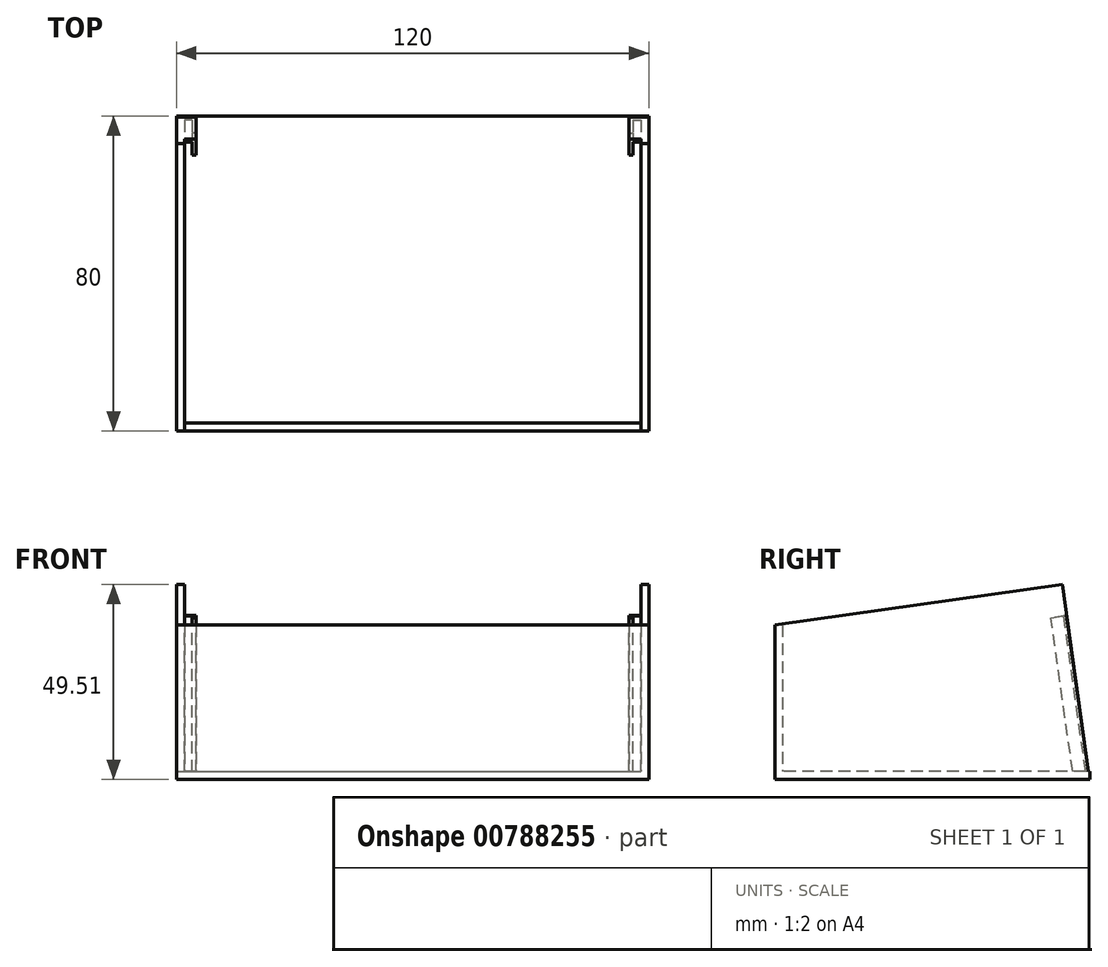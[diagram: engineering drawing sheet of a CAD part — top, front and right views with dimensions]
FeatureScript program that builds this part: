
annotation { "Feature Type Name" : "Feature", "Feature Type Description" : "" }
export const myFeature = defineFeature(function(context is Context, id is Id, definition is map)
    precondition{}
    {
        {
            var Q0;
            Q0=qCreatedBy(makeId("Top.planeOp"),FACE);
            var sketch = newSketch(context, id + "F0", { "sketchPlane" : qUnion([Q0])});
            skLineSegment(sketch, "E0.bottom", {"start": v(-60, 56.5) * mm, "end": v(60, 56.5) * mm});
            skLineSegment(sketch, "E0.top", {"start": v(-60, -23.5) * mm, "end": v(60, -23.5) * mm});
            skLineSegment(sketch, "E0.left", {"start": v(-60, 56.5) * mm, "end": v(-60, -23.5) * mm});
            skLineSegment(sketch, "E0.right", {"start": v(60, 56.5) * mm, "end": v(60, -23.5) * mm});
            skSolve(sketch);
        }
        {
            var Q0;
            Q0 = qSketchRegion(id + "F0", true);
            var Q1;
            Q1=makeQuery(id+"F0.imprint","IMPRINT",FACE,{"disambiguationData":[TD([[makeQuery(id+"F0.imprint","IMPRINT",EDGE,{"derivedFrom":sQuery(id+"F0.wireOp",EDGE,"E0.bottom")}),-1.0]])]});
            extrude(context, id + "F1", {"entities" : qUnion([Q0, Q1]), "depth" : 2 * mm, "offsetDistance" : 25 * mm});
        }
        {
            var Q0;
            Q0=makeQuery(id+"F1.opExtrude","SWEPT_FACE",FACE,{"disambiguationData":[OSD([sQuery(id+"F0.wireOp",EDGE,"E0.right")])]});
            var sketch = newSketch(context, id + "F2", { "sketchPlane" : qUnion([Q0])});
            skLineSegment(sketch, "E1", {"start": v(56.5, 0) * mm, "end": v(49.5, 49.5) * mm});
            skLineSegment(sketch, "E2", {"start": v(49.5, 49.5) * mm, "end": v(-23.5, 39.19) * mm});
            skLineSegment(sketch, "E3", {"start": v(-23.5, 39.19) * mm, "end": v(-23.5, 0) * mm});
            skSolve(sketch);
        }
        {
            var Q0;
            Q0 = qSketchRegion(id + "F2", true);
            var Q1;
            {var subQ0=sQuery(id+"F2.wireOp",EDGE,"E2");Q1=makeQuery(id+"F2.imprint","IMPRINT",FACE,{"disambiguationData":[TD([[makeQuery(id+"F2.imprint","IMPRINT",EDGE,{"derivedFrom":subQ0}),1.0]])]});}
            extrude(context, id + "F3", {"entities" : qUnion([Q0, Q1]), "operationType" : NewBodyOperationType.ADD, "oppositeDirection" : true, "depth" : 2 * mm, "offsetDistance" : 25 * mm});
        }
        {
            var Q0;
            Q0=makeQuery(id+"F1.opExtrude","SWEPT_BODY",BODY,{"disambiguationData":[OSD([sQuery(id+"F0.wireOp",EDGE,"E0.bottom"),sQuery(id+"F0.wireOp",EDGE,"E0.top"),sQuery(id+"F0.wireOp",EDGE,"E0.left"),sQuery(id+"F0.wireOp",EDGE,"E0.right")])]});
            var Q1;
            Q1=qCreatedBy(makeId("Right.planeOp"),FACE);
            mirror(context, id + "F4", {"operationType" : NewBodyOperationType.ADD, "entities" : qUnion([Q0]), "mirrorPlane" : qUnion([Q1])});
        }
        {
            var Q0;
            {var subQ0=makeQuery(id+"F3.boolean.opBoolean","MERGE",FACE,{"derivedFrom":[makeQuery(id+"F1.opExtrude","SWEPT_FACE",FACE,{"disambiguationData":[OSD([sQuery(id+"F0.wireOp",EDGE,"E0.top")])]}),makeQuery(id+"F3.opExtrude","SWEPT_FACE",FACE,{"disambiguationData":[OSD([sQuery(id+"F2.wireOp",EDGE,"E3")])]})]});Q0=makeQuery(id+"F4.boolean.opBoolean","MERGE",FACE,{"derivedFrom":[subQ0,makeQuery(id+"F4.opPattern","COPY",FACE,{"derivedFrom":subQ0,"instanceName":"1"})]});}
            var sketch = newSketch(context, id + "F5", { "sketchPlane" : qUnion([Q0])});
            skLineSegment(sketch, "E4", {"start": v(-60, 39.19) * mm, "end": v(-60, 0) * mm});
            skLineSegment(sketch, "E5", {"start": v(60, 39.19) * mm, "end": v(-60, 39.19) * mm});
            skSolve(sketch);
        }
        {
            var Q0;
            {var subQ1=makeQuery(id+"F3.opExtrude","CAP_EDGE",EDGE,{"disambiguationData":[OSD([sQuery(id+"F2.wireOp",EDGE,"E3")])],"isStart":false});Q0=makeQuery(id+"F5.imprint","IMPRINT",FACE,{"disambiguationData":[TD([[makeQuery(id+"F5.imprint","IMPRINT",EDGE,{"derivedFrom":subQ1}),-1.0]])]});}
            extrude(context, id + "F6", {"entities" : qUnion([Q0]), "operationType" : NewBodyOperationType.ADD, "oppositeDirection" : true, "depth" : 2 * mm, "offsetDistance" : 25 * mm});
        }
        {
            var Q0;
            Q0=makeQuery(id+"F4.opPattern","COPY",FACE,{"derivedFrom":makeQuery(id+"F3.opExtrude","CAP_FACE",FACE,{"disambiguationData":[OSD([sQuery(id+"F0.wireOp",EDGE,"E0.right"),sQuery(id+"F2.wireOp",EDGE,"E1"),sQuery(id+"F2.wireOp",EDGE,"E2"),sQuery(id+"F2.wireOp",EDGE,"E3")])],"isStart":false}),"instanceName":"1"});
            var sketch = newSketch(context, id + "F7", { "sketchPlane" : qUnion([Q0])});
            skLineSegment(sketch, "E6", {"start": v(56.22, 2) * mm, "end": v(50.62, 41.6) * mm});
            skLineSegment(sketch, "E7", {"start": v(50.62, 41.6) * mm, "end": v(46.66, 41.05) * mm});
            skLineSegment(sketch, "E8", {"start": v(46.66, 41.05) * mm, "end": v(52.18, 2) * mm});
            skSolve(sketch);
        }
        {
            var Q0;
            Q0 = qSketchRegion(id + "F7", true);
            var Q1;
            {var subQ0=sQuery(id+"F7.wireOp",EDGE,"E6");Q1=makeQuery(id+"F7.imprint","IMPRINT",FACE,{"disambiguationData":[TD([[makeQuery(id+"F7.imprint","IMPRINT",EDGE,{"derivedFrom":subQ0}),1.0]])]});}
            extrude(context, id + "F8", {"entities" : qUnion([Q0, Q1]), "operationType" : NewBodyOperationType.ADD, "depth" : 3 * mm, "offsetDistance" : 25 * mm});
        }
        {
            var Q0;
            Q0=makeQuery(id+"F8.opExtrude","SWEPT_FACE",FACE,{"disambiguationData":[OSD([sQuery(id+"F7.wireOp",EDGE,"E7")])]});
            var sketch = newSketch(context, id + "F9", { "sketchPlane" : qUnion([Q0])});
            skLineSegment(sketch, "E9.bottom", {"start": v(-58, 51.94) * mm, "end": v(-56, 51.94) * mm});
            skLineSegment(sketch, "E9.top", {"start": v(-58, 55.22) * mm, "end": v(-56, 55.22) * mm});
            skLineSegment(sketch, "E9.left", {"start": v(-58, 51.94) * mm, "end": v(-58, 55.22) * mm});
            skLineSegment(sketch, "E9.right", {"start": v(-56, 51.94) * mm, "end": v(-56, 55.22) * mm});
            skSolve(sketch);
        }
        {
            var Q0;
            Q0=makeQuery(id+"F9.imprint","IMPRINT",FACE,{"disambiguationData":[TD([[makeQuery(id+"F9.imprint","IMPRINT",EDGE,{"derivedFrom":sQuery(id+"F9.wireOp",EDGE,"E9.bottom")}),-1.0]])]});
            var Q1;
            Q1=makeQuery(id+"F1.opExtrude","CAP_FACE",FACE,{"disambiguationData":[OSD([sQuery(id+"F0.wireOp",EDGE,"E0.bottom"),sQuery(id+"F0.wireOp",EDGE,"E0.top"),sQuery(id+"F0.wireOp",EDGE,"E0.left"),sQuery(id+"F0.wireOp",EDGE,"E0.right")])],"isStart":false});
            extrude(context, id + "F10", {"entities" : qUnion([Q0]), "operationType" : NewBodyOperationType.REMOVE, "endBound" : BoundingType.UP_TO_SURFACE, "oppositeDirection" : true, "depth" : 25 * mm, "endBoundEntityFace" : qUnion([Q1]), "offsetDistance" : 25 * mm});
        }
        {
            var Q0;
            Q0=makeQuery(id+"F1.opExtrude","SWEPT_BODY",BODY,{"disambiguationData":[OSD([sQuery(id+"F0.wireOp",EDGE,"E0.bottom"),sQuery(id+"F0.wireOp",EDGE,"E0.top"),sQuery(id+"F0.wireOp",EDGE,"E0.left"),sQuery(id+"F0.wireOp",EDGE,"E0.right")])]});
            var Q1;
            Q1=qCreatedBy(makeId("Right.planeOp"),FACE);
            mirror(context, id + "F11", {"operationType" : NewBodyOperationType.ADD, "entities" : qUnion([Q0]), "mirrorPlane" : qUnion([Q1])});
        }
    });
